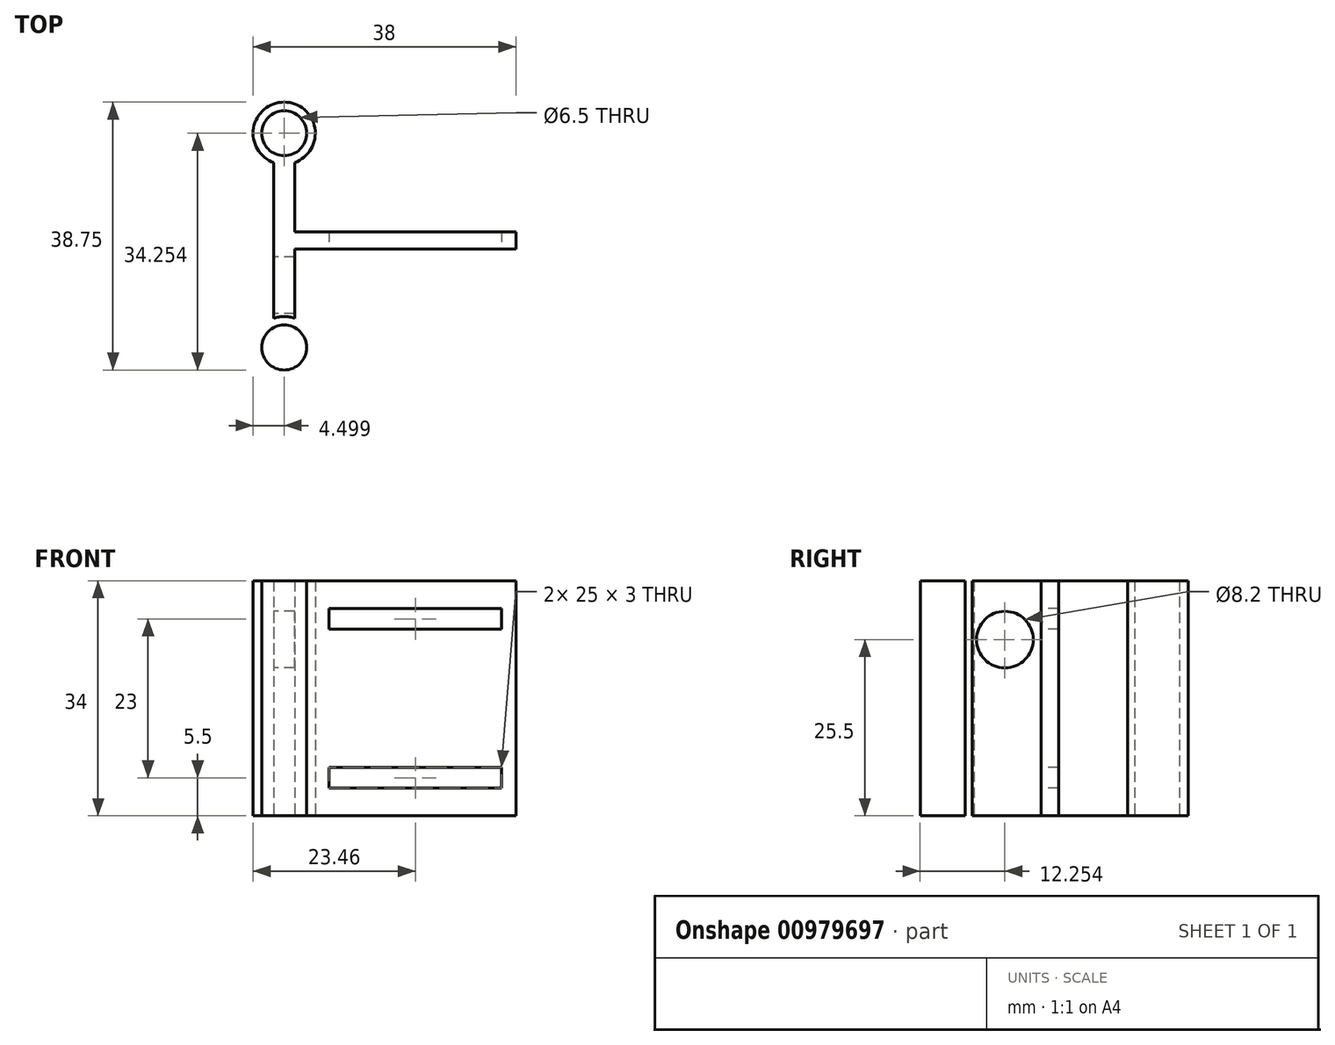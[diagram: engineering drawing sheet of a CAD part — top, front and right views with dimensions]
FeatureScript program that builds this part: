
annotation { "Feature Type Name" : "Feature", "Feature Type Description" : "" }
export const myFeature = defineFeature(function(context is Context, id is Id, definition is map)
    precondition{}
    {
        {
            var Q0;
            Q0=qCreatedBy(makeId("Top.planeOp"),FACE);
            var sketch = newSketch(context, id + "F0", { "sketchPlane" : qUnion([Q0])});
            skCircle(sketch, "E0", {"center": v(-31.46, 9.28) * mm, "radius": 3.25 * mm});
            skCircle(sketch, "E1", {"center": v(-31.46, 9.28) * mm, "radius": 4.5 * mm});
            skPoint(sketch, "E2.orphan", {"position": v(-29.92, -5.18) * mm});
            skPoint(sketch, "E3.MirrorP", {"position": v(-29.92, -7.68) * mm});
            skPoint(sketch, "E4.orphan", {"position": v(-13.43, 19.89) * mm});
            skPoint(sketch, "E5.end.orphan", {"position": v(-10.2, 19.3) * mm});
            skPoint(sketch, "E5.start.orphan", {"position": v(-11.82, 19.6) * mm});
            skPoint(sketch, "E6.start.orphan", {"position": v(-29.96, 5.04) * mm});
            skPoint(sketch, "E7.MirrorCS.start.orphan", {"position": v(-29.96, -17.9) * mm});
            skPoint(sketch, "E8.MirrorCS.end.orphan", {"position": v(2.04, -6.43) * mm});
            skPoint(sketch, "E9.end.orphan", {"position": v(2.04, -5.18) * mm});
            skPoint(sketch, "E9.start.orphan", {"position": v(-28.96, -5.18) * mm});
            skPoint(sketch, "E10.trimOffspring.end.orphan", {"position": v(15.86, -6.43) * mm});
            skPoint(sketch, "E11.end.orphan", {"position": v(15.86, -5.18) * mm});
            skPoint(sketch, "E12.orphan", {"position": v(15.86, -7.68) * mm});
            skPoint(sketch, "E13.start.orphan", {"position": v(-32.96, -6.43) * mm});
            skPoint(sketch, "E14.end.orphan", {"position": v(-32.96, -5.18) * mm});
            skPoint(sketch, "E14.start.orphan", {"position": v(-32.96, 5.04) * mm});
            skPoint(sketch, "E15.MirrorC.center.orphan", {"position": v(-30.96, -21.93) * mm});
            skLineSegment(sketch, "E16", {"start": v(-32.96, 5.04) * mm, "end": v(-32.96, -6.22) * mm});
            skLineSegment(sketch, "E17", {"start": v(-32.96, -6.22) * mm, "end": v(2.04, -6.22) * mm});
            skLineSegment(sketch, "E18", {"start": v(2.04, -6.22) * mm, "end": v(2.04, -4.97) * mm});
            skLineSegment(sketch, "E19", {"start": v(2.04, -4.97) * mm, "end": v(-29.96, -4.97) * mm});
            skLineSegment(sketch, "E20", {"start": v(-29.96, -4.97) * mm, "end": v(-29.96, 5.04) * mm});
            skLineSegment(sketch, "E21.MirrorCS", {"start": v(2.04, -6.22) * mm, "end": v(2.04, -7.47) * mm});
            skPoint(sketch, "E22.MirrorP", {"position": v(2.04, -6) * mm});
            skPoint(sketch, "E23.MirrorP", {"position": v(-29.96, 5.46) * mm});
            skPoint(sketch, "E24.MirrorP", {"position": v(-13.43, -32.32) * mm});
            skPoint(sketch, "E25.MirrorP", {"position": v(-29.92, -4.75) * mm});
            skPoint(sketch, "E26.MirrorP", {"position": v(15.86, -4.75) * mm});
            skPoint(sketch, "E27.MirrorP", {"position": v(-29.92, -7.25) * mm});
            skCircle(sketch, "E28.MirrorC", {"center": v(-31.46, -21.72) * mm, "radius": 3.25 * mm});
            skPoint(sketch, "E29.MirrorP", {"position": v(-11.82, -32.02) * mm});
            skPoint(sketch, "E30.MirrorP", {"position": v(-30.96, 9.5) * mm});
            skPoint(sketch, "E31.MirrorP", {"position": v(-28.96, -7.25) * mm});
            skCircle(sketch, "E32.MirrorC", {"center": v(-31.46, -21.72) * mm, "radius": 4.5 * mm});
            skLineSegment(sketch, "E33.MirrorCS", {"start": v(2.04, -7.47) * mm, "end": v(-29.96, -7.47) * mm});
            skPoint(sketch, "E34.MirrorP", {"position": v(2.04, -7.25) * mm});
            skPoint(sketch, "E35.MirrorP", {"position": v(-29.96, -17.47) * mm});
            skPoint(sketch, "E36.MirrorP", {"position": v(-32.96, -6) * mm});
            skPoint(sketch, "E37.MirrorP", {"position": v(-32.96, -7.25) * mm});
            skPoint(sketch, "E38.MirrorP", {"position": v(15.86, -7.25) * mm});
            skLineSegment(sketch, "E39.MirrorCS", {"start": v(-29.96, -7.47) * mm, "end": v(-29.96, -17.47) * mm});
            skPoint(sketch, "E40.MirrorP", {"position": v(15.86, -6) * mm});
            skLineSegment(sketch, "E41.MirrorCS", {"start": v(-32.96, -17.47) * mm, "end": v(-32.96, -6.22) * mm});
            skPoint(sketch, "E42.MirrorP", {"position": v(-32.96, -17.47) * mm});
            skPoint(sketch, "E43.MirrorP", {"position": v(-10.2, -31.72) * mm});
            skSolve(sketch);
        }
        {
            var Q0;
            Q0=makeQuery(id+"F0.imprint","IMPRINT",FACE,{"disambiguationData":[TD([[makeQuery(id+"F0.imprint","IMPRINT",EDGE,{"derivedFrom":sQuery(id+"F0.wireOp",EDGE,"E0")}),-1.0]])]});
            var Q1;
            {var subQ0=sQuery(id+"F0.wireOp",EDGE,"E16");Q1=makeQuery(id+"F0.imprint","IMPRINT",FACE,{"disambiguationData":[TD([[makeQuery(id+"F0.imprint","IMPRINT",EDGE,{"derivedFrom":subQ0}),1.0]])]});}
            var Q2;
            Q2=makeQuery(id+"F0.imprint","IMPRINT",FACE,{"disambiguationData":[TD([[makeQuery(id+"F0.imprint","IMPRINT",EDGE,{"derivedFrom":sQuery(id+"F0.wireOp",EDGE,"E17")}),-1.0]])]});
            var Q3;
            Q3=makeQuery(id+"F0.imprint","IMPRINT",FACE,{"disambiguationData":[TD([[makeQuery(id+"F0.imprint","IMPRINT",EDGE,{"derivedFrom":sQuery(id+"F0.wireOp",EDGE,"E28.MirrorC")}),1.0]])]});
            extrude(context, id + "F1", {"entities" : qUnion([Q0, Q1, Q2, Q3]), "depth" : 34 * mm, "offsetDistance" : 25 * mm});
        }
        {
            var Q0;
            Q0=makeQuery(id+"F1.opExtrude","SWEPT_FACE",FACE,{"disambiguationData":[OSD([sQuery(id+"F0.wireOp",EDGE,"E16"),sQuery(id+"F0.wireOp",EDGE,"E41.MirrorCS")])]});
            var sketch = newSketch(context, id + "F2", { "sketchPlane" : qUnion([Q0])});
            skPoint(sketch, "E44.orphan", {"position": v(6.22, 25.5) * mm});
            skPoint(sketch, "E45.end.orphan", {"position": v(17.47, 17) * mm});
            skPoint(sketch, "E46.start.orphan", {"position": v(6.22, 34) * mm});
            skPoint(sketch, "E47.end.orphan", {"position": v(6.22, 17) * mm});
            skPoint(sketch, "E47.start.orphan", {"position": v(6.22, 0) * mm});
            skPoint(sketch, "E48.center.orphan", {"position": v(11.84, 25.5) * mm});
            skLineSegment(sketch, "E49", {"start": v(6.22, 25.5) * mm, "end": v(12.72, 25.5) * mm});
            skCircle(sketch, "E50", {"center": v(12.72, 25.5) * mm, "radius": 4.1 * mm});
            skSolve(sketch);
        }
        {
            var Q0;
            Q0=makeQuery(id+"F2.imprint","IMPRINT",FACE,{"disambiguationData":[TD([[makeQuery(id+"F2.imprint","IMPRINT",EDGE,{"derivedFrom":sQuery(id+"F2.wireOp",EDGE,"E50")}),1.0]])]});
            extrude(context, id + "F3", {"entities" : qUnion([Q0]), "operationType" : NewBodyOperationType.REMOVE, "oppositeDirection" : true, "depth" : 25 * mm, "offsetDistance" : 25 * mm});
        }
        {
            var Q0;
            Q0=makeQuery(id+"F1.opExtrude","SWEPT_FACE",FACE,{"disambiguationData":[OSD([sQuery(id+"F0.wireOp",EDGE,"E33.MirrorCS")])]});
            var sketch = newSketch(context, id + "F4", { "sketchPlane" : qUnion([Q0])});
            skLineSegment(sketch, "E51.bottom", {"start": v(-25, 30) * mm, "end": v(0, 30) * mm});
            skLineSegment(sketch, "E51.top", {"start": v(-25, 27) * mm, "end": v(0, 27) * mm});
            skLineSegment(sketch, "E51.left", {"start": v(-25, 30) * mm, "end": v(-25, 27) * mm});
            skLineSegment(sketch, "E51.right", {"start": v(0, 30) * mm, "end": v(0, 27) * mm});
            skLineSegment(sketch, "E52.bottom", {"start": v(-25, 4) * mm, "end": v(0, 4) * mm});
            skLineSegment(sketch, "E52.top", {"start": v(-25, 7) * mm, "end": v(0, 7) * mm});
            skLineSegment(sketch, "E52.left", {"start": v(-25, 4) * mm, "end": v(-25, 7) * mm});
            skLineSegment(sketch, "E52.right", {"start": v(0, 4) * mm, "end": v(0, 7) * mm});
            skLineSegment(sketch, "E53.trimOffspring", {"start": v(-25, 7) * mm, "end": v(-25, 4) * mm});
            skSolve(sketch);
        }
        {
            var Q0;
            Q0=makeQuery(id+"F4.imprint","IMPRINT",FACE,{"disambiguationData":[TD([[makeQuery(id+"F4.imprint","IMPRINT",EDGE,{"derivedFrom":sQuery(id+"F4.wireOp",EDGE,"E51.bottom")}),-1.0]])]});
            var Q1;
            Q1=makeQuery(id+"F4.imprint","IMPRINT",FACE,{"disambiguationData":[TD([[makeQuery(id+"F4.imprint","IMPRINT",EDGE,{"derivedFrom":sQuery(id+"F4.wireOp",EDGE,"E52.bottom")}),1.0]])]});
            extrude(context, id + "F5", {"entities" : qUnion([Q0, Q1]), "operationType" : NewBodyOperationType.REMOVE, "oppositeDirection" : true, "depth" : 25 * mm, "offsetDistance" : 25 * mm});
        }
    });
